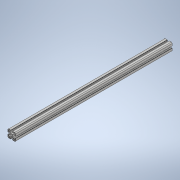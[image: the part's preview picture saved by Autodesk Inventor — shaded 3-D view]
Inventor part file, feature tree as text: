
AUTODESK INVENTOR PART (.ipt)
format: ipt  version: 2020 (Build 240168000, 168)  size: 221,696 bytes
history: native  units: mm
features: extrude x1, sketch x1
ambient origin geometry x8: Origin, YZ Plane, XZ Plane, XY Plane, X Axis, Y Axis, Z Axis, Center Point
bodies: Solid1 (feature_tree)
feature tree (2):
  extrude  "Extrusion1"  [1 undecoded]
  sketch  "Sketch1"  dims[d1=40.0mm d2=0.75mm d3=7.45mm d4=2.25mm d5=1.0mm d6=2.1mm d7=0.75mm d8=0.65mm d9=1.25mm d10=2.25mm d11=360.0deg d12=4.0mm d13=20.0mm d14=400.0mm d15=0.0mm]
note: 1 required parameter value undecoded (feature->parameter linkage not recoverable at this tier; creation-order binding heuristic only, values carry confidence <= 0.55)
